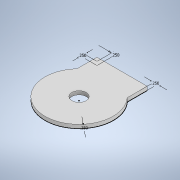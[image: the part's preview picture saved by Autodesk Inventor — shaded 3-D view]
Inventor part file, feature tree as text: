
AUTODESK INVENTOR PART (.ipt)
format: ipt  version: 2021.2 (Build 252289000, 289)  size: 129,024 bytes
history: native  units: in
note: dims shown in document units (in); Inventor stores cm internally (conversion verified against a paired STEP export)
features: extrude x3, sketch x2
ambient origin geometry x8: Origin, YZ Plane, XZ Plane, XY Plane, X Axis, Y Axis, Z Axis, Center Point
bodies: Solid1 (feature_tree)
feature tree (5):
  extrude  "Extrusion1"  Depth=0.25in TaperAngle=0.0deg
  extrude  "Extrusion4"  Depth=0.25in
  extrude  "Extrusion7"  Depth=0.25in
  sketch  "Sketch3"  dims[d0=4.25in d1=0.25in d2=0.0in]
  sketch  "Sketch5"  dims[d6=2.75in d7=1.5in d8=0.25in d9=0.25in d10=0.25in d11=0.25in d14=0.25in d15=0.0in d24=1.0in d25=0.0in d26=0.0in]
